# Revit family: Sink-Vanity_Top-Lavatory-KOHLER-Reach-K-18572IN_1
name_source: partatom
category: Plumbing Fixtures
units: mm (PartAtom-declared; Revit-internal decimal feet)

## family parameters
Cut with Voids When Loaded = No
Host = Face
OmniClass Number = 23.31.13.00
OmniClass Title = Sinks
Part Type = Normal
Room Calculation Point = No
Round Connector Dimension = Use Diameter
Shared = No

## types (1)
- 0-White
    ADA Compliant = No
    Assembly Code = D2010400
    CW Connection = No
    Cold Water Inlet = Cold Water Inlet
    Date Modified = 07/04/2023
    Default Elevation = 36"
    Description = VANITY TOP 70 CM W GOV
    Drain Included = No
    Finish = KOHLER-Fireclay-0-White
    Flow Rate = 0 GPM
    HW Connection = No
    Height = 7 3/8"
    Hot Water Inlet = Hot Water Inlet
    Length = 27 9/16"
    Manufacturer = Kohler Co.
    Master Format 2014 = 22 41 16
    Master Format 2014 Name = Residential Lavatories and Sinks
    Material = Fireclay
    Model = K-18572IN-XBV-0
    Pressure = 0.00 psi
    Product Name = Reach
    Type = 1
    URL = https://www.kohler.co.in
    Vent Connection = No
    Waste Connection = Yes
    Waste Water Outlet = Waste Water Outlet
    WaterSense Certified = No
    Width = 19 11/16"

## geometry (parser evidence)
native form markers: Sweep x6
no freeform markers — native parametric forms only
